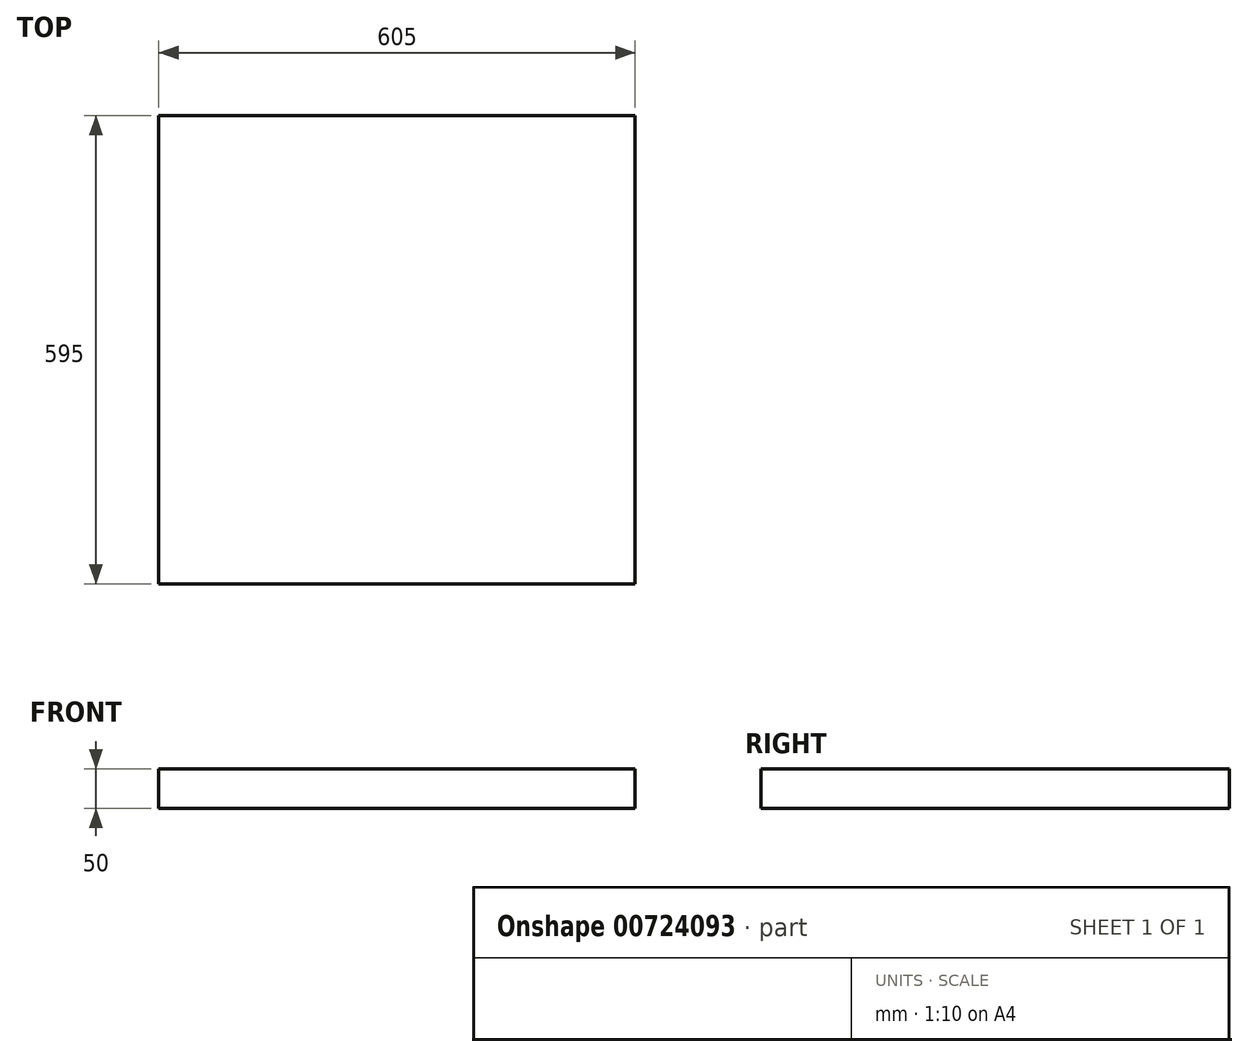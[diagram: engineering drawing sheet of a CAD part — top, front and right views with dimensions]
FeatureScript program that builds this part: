
annotation { "Feature Type Name" : "Feature", "Feature Type Description" : "" }
export const myFeature = defineFeature(function(context is Context, id is Id, definition is map)
    precondition{}
    {
        {
            var Q0;
            Q0=qCreatedBy(makeId("Top.planeOp"),FACE);
            var sketch = newSketch(context, id + "F0", { "sketchPlane" : qUnion([Q0])});
            skLineSegment(sketch, "E0.bottom", {"start": v(-300.4, 328.21) * mm, "end": v(304.6, 328.21) * mm});
            skLineSegment(sketch, "E0.top", {"start": v(-300.4, -266.79) * mm, "end": v(304.6, -266.79) * mm});
            skLineSegment(sketch, "E0.left", {"start": v(-300.4, 328.21) * mm, "end": v(-300.4, -266.79) * mm});
            skLineSegment(sketch, "E0.right", {"start": v(304.6, 328.21) * mm, "end": v(304.6, -266.79) * mm});
            skSolve(sketch);
        }
        {
            var Q0;
            Q0=qSketchRegion(id+"F0",true);
            extrude(context, id + "F1", {"entities" : qUnion([Q0]), "oppositeDirection" : true, "depth" : 50 * mm, "offsetDistance" : 25 * mm});
        }
    });
